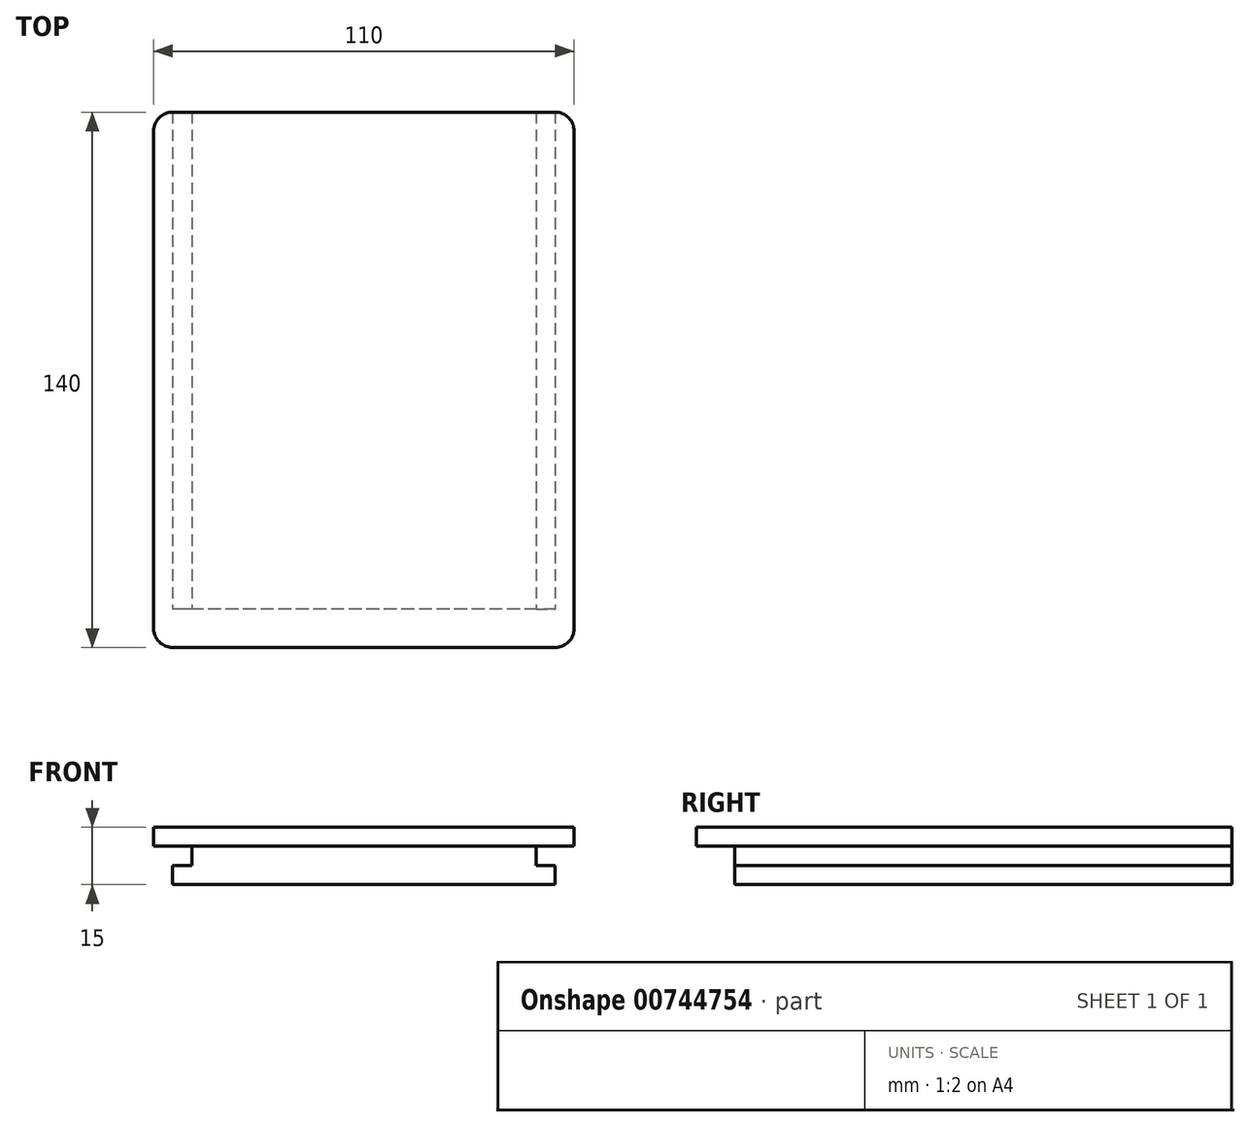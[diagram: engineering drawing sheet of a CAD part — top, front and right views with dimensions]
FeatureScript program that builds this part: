
annotation { "Feature Type Name" : "Feature", "Feature Type Description" : "" }
export const myFeature = defineFeature(function(context is Context, id is Id, definition is map)
    precondition{}
    {
        {
            var Q0;
            Q0=qCreatedBy(makeId("Top.planeOp"),FACE);
            var sketch = newSketch(context, id + "F0", { "sketchPlane" : qUnion([Q0])});
            skLineSegment(sketch, "E0.bottom", {"start": v(50, 70) * mm, "end": v(-50, 70) * mm});
            skLineSegment(sketch, "E0.top", {"start": v(50, -70) * mm, "end": v(-50, -70) * mm});
            skLineSegment(sketch, "E0.left", {"start": v(55, 65) * mm, "end": v(55, -65) * mm});
            skLineSegment(sketch, "E0.right", {"start": v(-55, 65) * mm, "end": v(-55, -65) * mm});
            skPoint(sketch, "E0.middle", {"position": v(0, 0) * mm});
            skPoint(sketch, "E1.visualSharp", {"position": v(55, 70) * mm});
            skArc(sketch, "E1.filletArc", {"start": v(55, 65) * mm, "mid": v(53.54, 68.54) * mm, "end": v(50, 70) * mm});
            skPoint(sketch, "E2.visualSharp", {"position": v(55, -70) * mm});
            skArc(sketch, "E2.filletArc", {"start": v(50, -70) * mm, "mid": v(53.54, -68.54) * mm, "end": v(55, -65) * mm});
            skPoint(sketch, "E3.visualSharp", {"position": v(-55, -70) * mm});
            skArc(sketch, "E3.filletArc", {"start": v(-55, -65) * mm, "mid": v(-53.54, -68.54) * mm, "end": v(-50, -70) * mm});
            skPoint(sketch, "E4.visualSharp", {"position": v(-55, 70) * mm});
            skArc(sketch, "E4.filletArc", {"start": v(-50, 70) * mm, "mid": v(-53.54, 68.54) * mm, "end": v(-55, 65) * mm});
            skSolve(sketch);
        }
        {
            var Q0;
            Q0=makeQuery(id+"F0.imprint","IMPRINT",FACE,{"disambiguationData":[TD([[makeQuery(id+"F0.imprint","IMPRINT",EDGE,{"derivedFrom":sQuery(id+"F0.wireOp",EDGE,"E0.bottom")}),1.0]])]});
            extrude(context, id + "F1", {"entities" : qUnion([Q0]), "depth" : 15 * mm, "offsetDistance" : 25 * mm});
        }
        {
            var Q0;
            Q0=qCreatedBy(makeId("Front.planeOp"),FACE);
            var sketch = newSketch(context, id + "F2", { "sketchPlane" : qUnion([Q0])});
            skLineSegment(sketch, "E5.bottom", {"start": v(-45, 5) * mm, "end": v(-55, 5) * mm});
            skLineSegment(sketch, "E5.top", {"start": v(-45, 10) * mm, "end": v(-55, 10) * mm});
            skLineSegment(sketch, "E5.left", {"start": v(-45, 5) * mm, "end": v(-45, 10) * mm});
            skLineSegment(sketch, "E5.right", {"start": v(-55, 5) * mm, "end": v(-55, 10) * mm});
            skPoint(sketch, "E5.middle", {"position": v(-50, 7.5) * mm});
            skLineSegment(sketch, "E6.bottom", {"start": v(-55, 5) * mm, "end": v(-50, 5) * mm});
            skLineSegment(sketch, "E6.top", {"start": v(-55, 0) * mm, "end": v(-50, 0) * mm});
            skLineSegment(sketch, "E6.left", {"start": v(-55, 5) * mm, "end": v(-55, 0) * mm});
            skLineSegment(sketch, "E6.right", {"start": v(-50, 5) * mm, "end": v(-50, 0) * mm});
            skPoint(sketch, "E7.MirrorP", {"position": v(50, 7.5) * mm});
            skLineSegment(sketch, "E8.MirrorCS", {"start": v(55, 0) * mm, "end": v(50, 0) * mm});
            skLineSegment(sketch, "E9.MirrorCS", {"start": v(45, 5) * mm, "end": v(55, 5) * mm});
            skLineSegment(sketch, "E10.MirrorCS", {"start": v(55, 5) * mm, "end": v(55, 0) * mm});
            skLineSegment(sketch, "E11.MirrorCS", {"start": v(45, 5) * mm, "end": v(45, 10) * mm});
            skLineSegment(sketch, "E12.MirrorCS", {"start": v(50, 5) * mm, "end": v(50, 0) * mm});
            skLineSegment(sketch, "E13.MirrorCS", {"start": v(55, 5) * mm, "end": v(50, 5) * mm});
            skLineSegment(sketch, "E14.MirrorCS", {"start": v(45, 10) * mm, "end": v(55, 10) * mm});
            skLineSegment(sketch, "E15.MirrorCS", {"start": v(55, 5) * mm, "end": v(55, 10) * mm});
            skSolve(sketch);
        }
        {
            var Q0;
            Q0 = qSketchRegion(id + "F2", true);
            extrude(context, id + "F3", {"entities" : qUnion([Q0]), "operationType" : NewBodyOperationType.REMOVE, "endBound" : BoundingType.SYMMETRIC, "oppositeDirection" : true, "depth" : 140 * mm, "offsetDistance" : 25 * mm});
        }
        {
            var Q0;
            Q0=makeQuery(id+"F1.opExtrude","SWEPT_FACE",FACE,{"disambiguationData":[OSD([sQuery(id+"F0.wireOp",EDGE,"E0.top")])]});
            var sketch = newSketch(context, id + "F4", { "sketchPlane" : qUnion([Q0])});
            skLineSegment(sketch, "E16.bottom", {"start": v(50, 0) * mm, "end": v(-50, 0) * mm});
            skLineSegment(sketch, "E16.top", {"start": v(50, 10) * mm, "end": v(-50, 10) * mm});
            skLineSegment(sketch, "E16.left", {"start": v(50, 0) * mm, "end": v(50, 10) * mm});
            skLineSegment(sketch, "E16.right", {"start": v(-50, 0) * mm, "end": v(-50, 10) * mm});
            skSolve(sketch);
        }
        {
            var Q0;
            {var subQ1=sQuery(id+"F4.wireOp",EDGE,"E16.bottom");Q0=makeQuery(id+"F4.imprint","IMPRINT",FACE,{"disambiguationData":[TD([[makeQuery(id+"F4.imprint","IMPRINT",EDGE,{"derivedFrom":subQ1}),-1.0]])]});}
            extrude(context, id + "F5", {"entities" : qUnion([Q0]), "operationType" : NewBodyOperationType.REMOVE, "oppositeDirection" : true, "depth" : 10 * mm, "offsetDistance" : 25 * mm});
        }
    });
